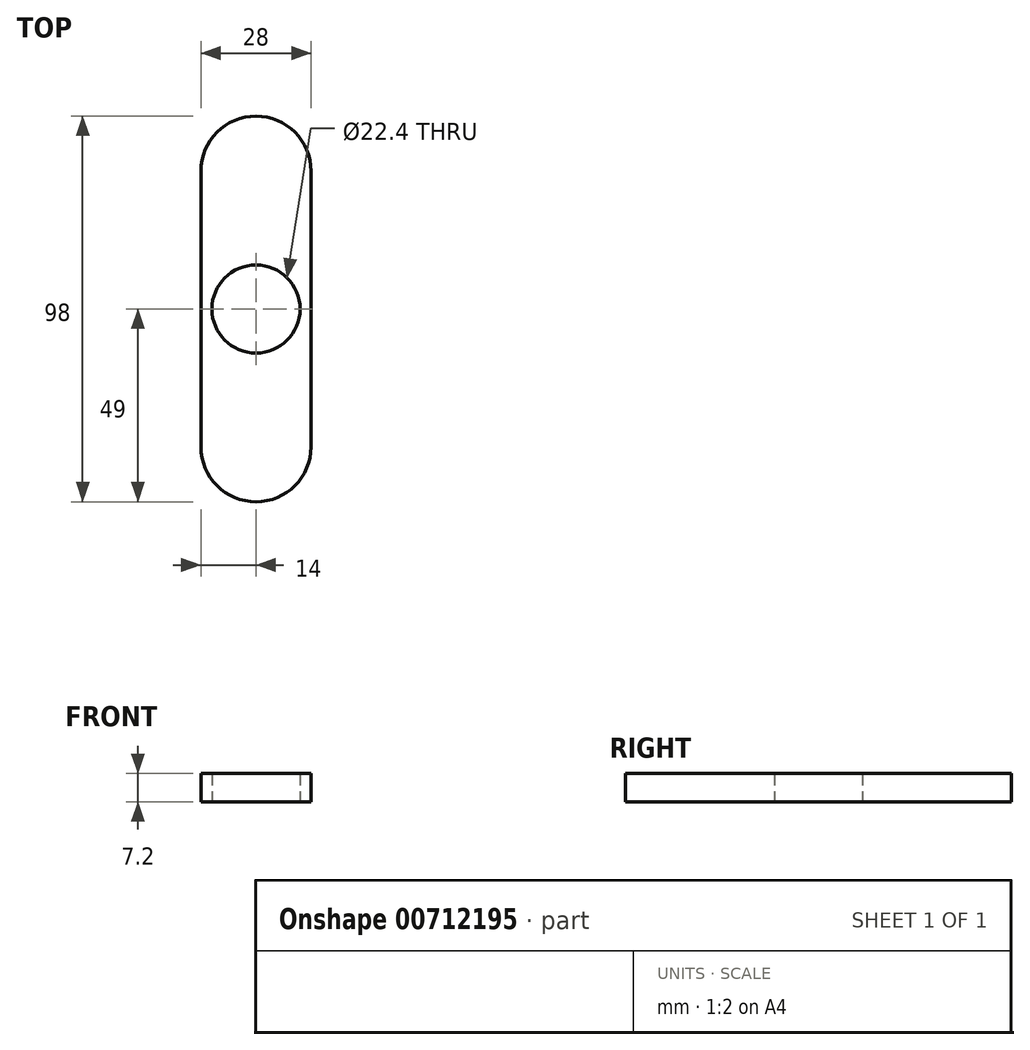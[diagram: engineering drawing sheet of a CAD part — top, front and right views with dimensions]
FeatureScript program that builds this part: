
annotation { "Feature Type Name" : "Feature", "Feature Type Description" : "" }
export const myFeature = defineFeature(function(context is Context, id is Id, definition is map)
    precondition{}
    {
        {
            var Q0;
            Q0=qCreatedBy(makeId("Top.planeOp"),FACE);
            var sketch = newSketch(context, id + "F0", { "sketchPlane" : qUnion([Q0])});
            skCircle(sketch, "E0", {"center": v(0, 0) * mm, "radius": 11.2 * mm});
            skCircle(sketch, "E1", {"center": v(0, 0) * mm, "radius": 14 * mm});
            skLineSegment(sketch, "E2", {"start": v(-14, 0) * mm, "end": v(-14, 35) * mm});
            skPoint(sketch, "E3", {"position": v(14, 0) * mm});
            skLineSegment(sketch, "E4", {"start": v(14, 0) * mm, "end": v(14, 35) * mm});
            skArc(sketch, "E5", {"start": v(14, 35) * mm, "mid": v(0, 49) * mm, "end": v(-14, 35) * mm});
            skLineSegment(sketch, "E6.1.0", {"start": v(14, 0) * mm, "end": v(14, -35) * mm});
            skLineSegment(sketch, "E7.1.0", {"start": v(-14, 0) * mm, "end": v(-14, -35) * mm});
            skArc(sketch, "E8.1.0", {"start": v(-14, -35) * mm, "mid": v(0, -49) * mm, "end": v(14, -35) * mm});
            skSolve(sketch);
        }
        {
            var Q0;
            {var subQ0=sQuery(id+"F0.wireOp",EDGE,"E2");Q0=makeQuery(id+"F0.imprint","IMPRINT",FACE,{"disambiguationData":[TD([[makeQuery(id+"F0.imprint","IMPRINT",EDGE,{"derivedFrom":subQ0}),-1.0]])]});}
            var Q1;
            Q1=makeQuery(id+"F0.imprint","IMPRINT",FACE,{"disambiguationData":[TD([[makeQuery(id+"F0.imprint","IMPRINT",EDGE,{"derivedFrom":sQuery(id+"F0.wireOp",EDGE,"E0")}),-1.0]])]});
            var Q2;
            {var subQ2=sQuery(id+"F0.wireOp",EDGE,"E6.1.0");Q2=makeQuery(id+"F0.imprint","IMPRINT",FACE,{"disambiguationData":[TD([[makeQuery(id+"F0.imprint","IMPRINT",EDGE,{"derivedFrom":subQ2}),-1.0]])]});}
            extrude(context, id + "F1", {"entities" : qUnion([Q0, Q1, Q2]), "depth" : 7.2 * mm, "offsetDistance" : 25 * mm});
        }
    });
